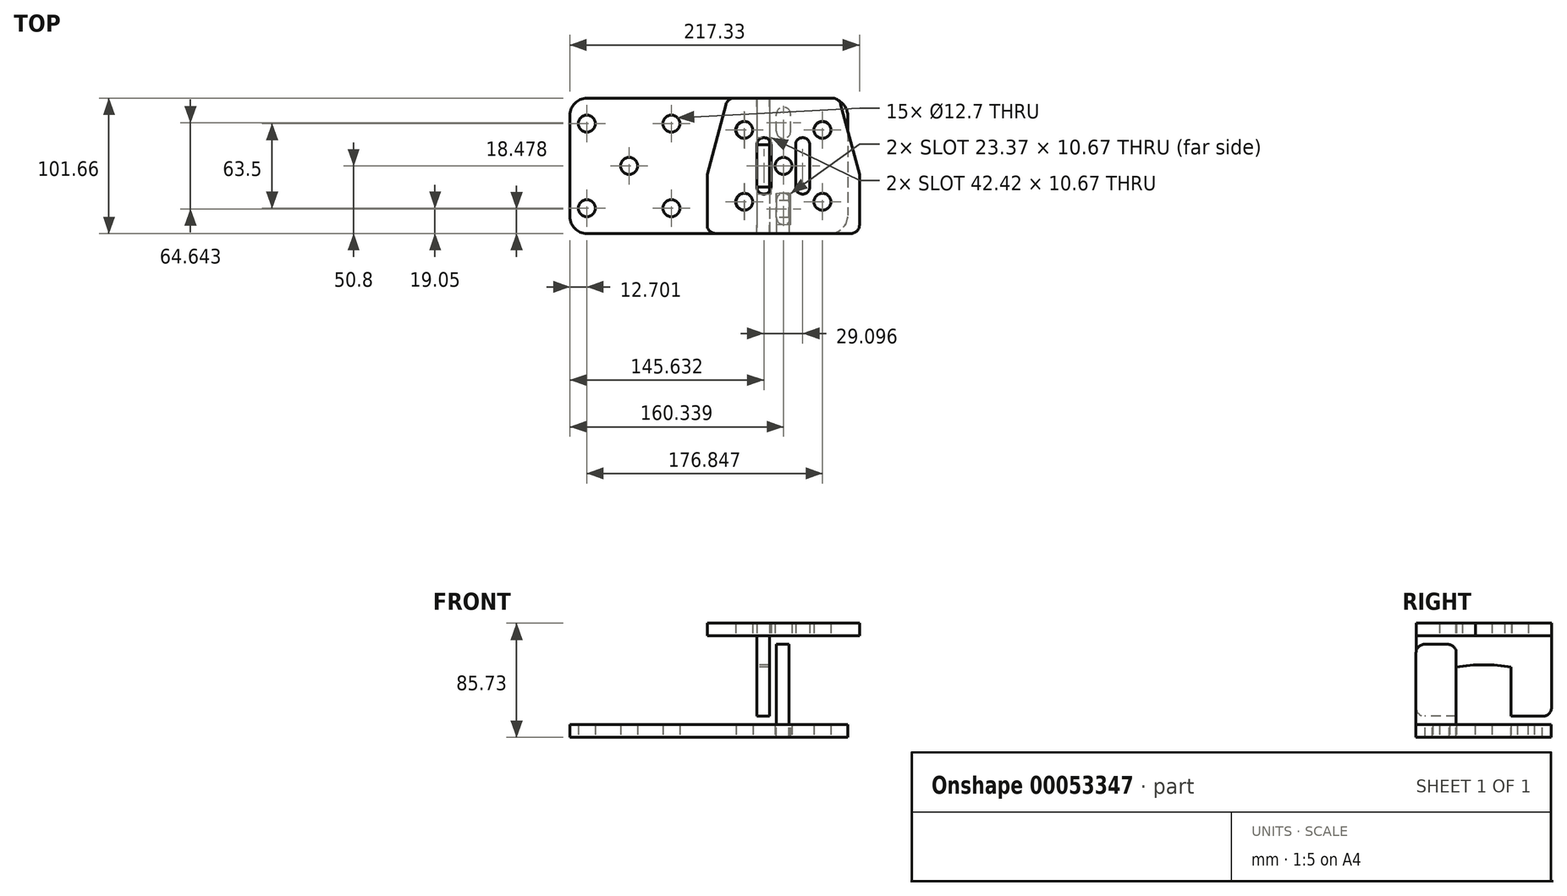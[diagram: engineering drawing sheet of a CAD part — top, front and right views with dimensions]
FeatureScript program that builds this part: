
annotation { "Feature Type Name" : "Feature", "Feature Type Description" : "" }
export const myFeature = defineFeature(function(context is Context, id is Id, definition is map)
    precondition{}
    {
        {
            var Q0;
            Q0=qCreatedBy(makeId("Top.planeOp"),FACE);
            var sketch = newSketch(context, id + "F0", { "sketchPlane" : qUnion([Q0])});
            skLineSegment(sketch, "E0.bottom", {"start": v(-84.85, -50.8) * mm, "end": v(97.55, -50.8) * mm});
            skLineSegment(sketch, "E0.top", {"start": v(-84.85, 50.8) * mm, "end": v(97.55, 50.8) * mm});
            skPoint(sketch, "E0.middle", {"position": v(0, 0) * mm});
            skCircle(sketch, "E1", {"center": v(-84.85, 31.75) * mm, "radius": 6.35 * mm});
            skCircle(sketch, "E2.0.1.0", {"center": v(-84.85, -31.75) * mm, "radius": 6.35 * mm});
            skCircle(sketch, "E2.1.0.0", {"center": v(-21.35, 31.75) * mm, "radius": 6.35 * mm});
            skCircle(sketch, "E2.1.1.0", {"center": v(-21.35, -31.75) * mm, "radius": 6.35 * mm});
            skLineSegment(sketch, "E2.direction1", {"start": v(-84.85, 31.75) * mm, "end": v(-21.35, 31.75) * mm, "construction": true});
            skLineSegment(sketch, "E2.direction2", {"start": v(-84.85, 31.75) * mm, "end": v(-84.85, -31.75) * mm, "construction": true});
            skLineSegment(sketch, "E3", {"start": v(-97.55, 0) * mm, "end": v(-84.85, 0) * mm, "construction": true});
            skPoint(sketch, "E4.visualSharp", {"position": v(-97.55, -50.8) * mm});
            skArc(sketch, "E4.filletArc", {"start": v(-97.55, -38.1) * mm, "mid": v(-93.83, -47.08) * mm, "end": v(-84.85, -50.8) * mm});
            skCircle(sketch, "E5", {"center": v(33.58, 26.92) * mm, "radius": 6.35 * mm});
            skCircle(sketch, "E6.0.1.0", {"center": v(33.58, -26.92) * mm, "radius": 6.35 * mm});
            skCircle(sketch, "E6.1.0.0", {"center": v(92, 26.92) * mm, "radius": 6.35 * mm});
            skCircle(sketch, "E6.1.1.0", {"center": v(92, -26.92) * mm, "radius": 6.35 * mm});
            skLineSegment(sketch, "E6.direction1", {"start": v(33.58, 26.92) * mm, "end": v(92, 26.92) * mm, "construction": true});
            skLineSegment(sketch, "E6.direction2", {"start": v(33.58, 26.92) * mm, "end": v(33.58, -26.92) * mm, "construction": true});
            skLineSegment(sketch, "E7", {"start": v(400.93, 50.8) * mm, "end": v(400.93, -50.8) * mm, "construction": true});
            skCircle(sketch, "E8", {"center": v(-53.1, 0) * mm, "radius": 6.35 * mm});
            skCircle(sketch, "E9", {"center": v(62.79, 0) * mm, "radius": 6.35 * mm});
            skPoint(sketch, "E9.centerSnap0", {"position": v(33.58, 0) * mm});
            skPoint(sketch, "E10", {"position": v(-53.1, 31.75) * mm});
            skPoint(sketch, "E11", {"position": v(62.79, 26.92) * mm});
            skCircle(sketch, "E12.MirrorC", {"center": v(854.95, 0) * mm, "radius": 6.35 * mm});
            skCircle(sketch, "E13.MirrorC", {"center": v(768.27, 26.92) * mm, "radius": 6.35 * mm});
            skArc(sketch, "E14.MirrorCS", {"start": v(899.4, -38.1) * mm, "mid": v(895.68, -47.08) * mm, "end": v(886.7, -50.8) * mm});
            skLineSegment(sketch, "E15.MirrorCS", {"start": v(899.4, 0) * mm, "end": v(886.7, 0) * mm, "construction": true});
            skLineSegment(sketch, "E16.MirrorCS", {"start": v(886.7, 31.75) * mm, "end": v(823.2, 31.75) * mm, "construction": true});
            skLineSegment(sketch, "E17.MirrorCS", {"start": v(768.27, 26.92) * mm, "end": v(709.85, 26.92) * mm, "construction": true});
            skCircle(sketch, "E18.MirrorC", {"center": v(823.2, -31.75) * mm, "radius": 6.35 * mm});
            skPoint(sketch, "E19.MirrorP", {"position": v(768.27, 0) * mm});
            skCircle(sketch, "E20.MirrorC", {"center": v(823.2, 31.75) * mm, "radius": 6.35 * mm});
            skCircle(sketch, "E21.MirrorC", {"center": v(886.7, -31.75) * mm, "radius": 6.35 * mm});
            skCircle(sketch, "E22.MirrorC", {"center": v(886.7, 31.75) * mm, "radius": 6.35 * mm});
            skPoint(sketch, "E23.MirrorP", {"position": v(739.06, 26.92) * mm});
            skLineSegment(sketch, "E24.MirrorCS", {"start": v(704.3, -50.8) * mm, "end": v(704.3, 50.8) * mm});
            skLineSegment(sketch, "E25.MirrorCS", {"start": v(899.4, -38.1) * mm, "end": v(899.4, 50.8) * mm});
            skPoint(sketch, "E26.MirrorP", {"position": v(854.95, 31.75) * mm});
            skLineSegment(sketch, "E27.MirrorCS", {"start": v(899.4, 50.8) * mm, "end": v(704.3, 50.8) * mm});
            skCircle(sketch, "E28.MirrorC", {"center": v(739.06, 0) * mm, "radius": 6.35 * mm});
            skCircle(sketch, "E29.MirrorC", {"center": v(709.85, -26.92) * mm, "radius": 6.35 * mm});
            skPoint(sketch, "E30.MirrorP", {"position": v(899.4, -50.8) * mm});
            skCircle(sketch, "E31.MirrorC", {"center": v(768.27, -26.92) * mm, "radius": 6.35 * mm});
            skLineSegment(sketch, "E32.MirrorCS", {"start": v(886.7, 31.75) * mm, "end": v(886.7, -31.75) * mm, "construction": true});
            skLineSegment(sketch, "E33.MirrorCS", {"start": v(768.27, 26.92) * mm, "end": v(768.27, -26.92) * mm, "construction": true});
            skCircle(sketch, "E34.MirrorC", {"center": v(709.85, 26.92) * mm, "radius": 6.35 * mm});
            skPoint(sketch, "E35.MirrorP", {"position": v(801.85, 0) * mm});
            skLineSegment(sketch, "E36.MirrorCS", {"start": v(886.7, -50.8) * mm, "end": v(704.3, -50.8) * mm});
            skLineSegment(sketch, "E37", {"start": v(111.05, 37.3) * mm, "end": v(111.05, -37.3) * mm});
            skArc(sketch, "E38", {"start": v(111.05, 37.3) * mm, "mid": v(107.1, 46.85) * mm, "end": v(97.55, 50.8) * mm});
            skArc(sketch, "E39", {"start": v(97.55, -50.8) * mm, "mid": v(107.1, -46.85) * mm, "end": v(111.05, -37.3) * mm});
            skCircle(sketch, "E40.MirrorC", {"center": v(972.43, 50.8) * mm, "radius": 6.35 * mm});
            skPoint(sketch, "E41.startSnap0", {"position": v(0, 50.8) * mm});
            skPoint(sketch, "E42.orphan", {"position": v(-97.55, 50.8) * mm});
            skPoint(sketch, "E43.visualSharp", {"position": v(-53.1, 50.8) * mm});
            skLineSegment(sketch, "E44", {"start": v(-97.55, -38.1) * mm, "end": v(-97.55, 38.1) * mm});
            skPoint(sketch, "E45.visualSharp", {"position": v(-97.55, 0) * mm});
            skArc(sketch, "E46.filletArc", {"start": v(-84.85, 50.8) * mm, "mid": v(-93.83, 47.08) * mm, "end": v(-97.55, 38.1) * mm});
            skSolve(sketch);
        }
        {
            var Q0;
            Q0=makeQuery(id+"F0.imprint","IMPRINT",FACE,{"disambiguationData":[TD([[makeQuery(id+"F0.imprint","IMPRINT",EDGE,{"derivedFrom":sQuery(id+"F0.wireOp",EDGE,"E0.bottom")}),1.0]])]});
            extrude(context, id + "F1", {"entities" : qUnion([Q0]), "depth" : 9.52 * mm});
        }
        {
            var Q0;
            Q0=makeQuery(id+"F1.opExtrude","CAP_FACE",FACE,{"disambiguationData":[OSD([sQuery(id+"F0.wireOp",EDGE,"E0.bottom"),sQuery(id+"F0.wireOp",EDGE,"E0.top"),sQuery(id+"F0.wireOp",EDGE,"E1"),sQuery(id+"F0.wireOp",EDGE,"E2.0.1.0"),sQuery(id+"F0.wireOp",EDGE,"E2.1.0.0"),sQuery(id+"F0.wireOp",EDGE,"E2.1.1.0"),sQuery(id+"F0.wireOp",EDGE,"E4.filletArc"),sQuery(id+"F0.wireOp",EDGE,"E5"),sQuery(id+"F0.wireOp",EDGE,"E6.0.1.0"),sQuery(id+"F0.wireOp",EDGE,"E6.1.0.0"),sQuery(id+"F0.wireOp",EDGE,"E6.1.1.0"),sQuery(id+"F0.wireOp",EDGE,"E8"),sQuery(id+"F0.wireOp",EDGE,"E9"),sQuery(id+"F0.wireOp",EDGE,"E37"),sQuery(id+"F0.wireOp",EDGE,"E38"),sQuery(id+"F0.wireOp",EDGE,"E39"),sQuery(id+"F0.wireOp",EDGE,"E44"),sQuery(id+"F0.wireOp",EDGE,"E46.filletArc")])],"isStart":false});
            var sketch = newSketch(context, id + "F2", { "sketchPlane" : qUnion([Q0])});
            skLineSegment(sketch, "E47", {"start": v(62.79, 25.97) * mm, "end": v(62.79, 38.67) * mm, "construction": true});
            skLineSegment(sketch, "E48", {"start": v(62.79, -38.67) * mm, "end": v(62.79, -25.97) * mm, "construction": true});
            skPoint(sketch, "E49.orphan", {"position": v(62.79, 0) * mm});
            skArc(sketch, "E50.0.startCap", {"start": v(68.12, 25.97) * mm, "mid": v(62.79, 20.64) * mm, "end": v(57.45, 25.97) * mm});
            skArc(sketch, "E50.0.endCap", {"start": v(57.45, 38.67) * mm, "mid": v(62.79, 44) * mm, "end": v(68.12, 38.67) * mm});
            skLineSegment(sketch, "E50.0.left", {"start": v(57.45, 25.97) * mm, "end": v(57.45, 38.67) * mm});
            skLineSegment(sketch, "E50.0.right", {"start": v(68.12, 25.97) * mm, "end": v(68.12, 38.67) * mm});
            skArc(sketch, "E50.1.startCap", {"start": v(68.12, -38.67) * mm, "mid": v(62.79, -44) * mm, "end": v(57.45, -38.67) * mm});
            skArc(sketch, "E50.1.endCap", {"start": v(57.45, -25.97) * mm, "mid": v(62.79, -20.64) * mm, "end": v(68.12, -25.97) * mm});
            skLineSegment(sketch, "E50.1.left", {"start": v(57.45, -38.67) * mm, "end": v(57.45, -25.97) * mm});
            skLineSegment(sketch, "E50.1.right", {"start": v(68.12, -38.67) * mm, "end": v(68.12, -25.97) * mm});
            skLineSegment(sketch, "E51.bottom", {"start": v(56.06, -20.64) * mm, "end": v(69.52, -20.64) * mm, "construction": true});
            skLineSegment(sketch, "E51.top", {"start": v(56.06, 20.64) * mm, "end": v(69.52, 20.64) * mm, "construction": true});
            skLineSegment(sketch, "E51.left", {"start": v(56.06, -20.64) * mm, "end": v(56.06, 20.64) * mm, "construction": true});
            skLineSegment(sketch, "E51.right", {"start": v(69.52, -20.64) * mm, "end": v(69.52, 20.64) * mm, "construction": true});
            skSolve(sketch);
        }
        {
            var Q0;
            Q0 = qSketchRegion(id + "F2", true);
            extrude(context, id + "F3", {"entities" : qUnion([Q0]), "operationType" : NewBodyOperationType.REMOVE, "oppositeDirection" : true, "depth" : 25.4 * mm});
        }
        {
            var Q0;
            Q0=qCreatedBy(makeId("Top.planeOp"),FACE);
            cPlane(context, id + "F4", {"entities" : qUnion([Q0]), "cplaneType" : CPlaneType.OFFSET, "offset" : 76.2 * mm, "width" : 152.4 * mm, "height" : 152.4 * mm});
        }
        {
            var Q0;
            Q0=qCreatedBy(id+"F4.planeOp",FACE);
            var sketch = newSketch(context, id + "F5", { "sketchPlane" : qUnion([Q0])});
            skArc(sketch, "E52", {"start": v(25.67, 50.86) * mm, "mid": v(21.8, 49.55) * mm, "end": v(19.53, 46.16) * mm});
            skArc(sketch, "E53", {"start": v(105.73, 46.16) * mm, "mid": v(103.46, 49.55) * mm, "end": v(99.6, 50.86) * mm});
            skArc(sketch, "E54", {"start": v(5.48, -44.39) * mm, "mid": v(7.34, -48.88) * mm, "end": v(11.83, -50.74) * mm});
            skArc(sketch, "E55", {"start": v(113.43, -50.74) * mm, "mid": v(117.92, -48.88) * mm, "end": v(119.78, -44.39) * mm});
            skCircle(sketch, "E56", {"center": v(62.79, 0) * mm, "radius": 6.35 * mm});
            skCircle(sketch, "E57", {"center": v(33.26, 27.05) * mm, "radius": 6.35 * mm});
            skCircle(sketch, "E58", {"center": v(92, 27.05) * mm, "radius": 6.35 * mm});
            skCircle(sketch, "E59", {"center": v(33.26, -26.92) * mm, "radius": 6.35 * mm});
            skCircle(sketch, "E60", {"center": v(92, -26.92) * mm, "radius": 6.35 * mm});
            skLineSegment(sketch, "E61", {"start": v(113.43, -50.74) * mm, "end": v(11.83, -50.74) * mm});
            skLineSegment(sketch, "E62", {"start": v(99.6, 50.86) * mm, "end": v(25.67, 50.86) * mm});
            skLineSegment(sketch, "E63", {"start": v(5.48, -44.39) * mm, "end": v(5.48, -6.29) * mm});
            skLineSegment(sketch, "E64", {"start": v(119.78, -44.39) * mm, "end": v(119.78, -6.29) * mm});
            skLineSegment(sketch, "E65", {"start": v(19.53, 46.16) * mm, "end": v(5.48, -6.29) * mm});
            skLineSegment(sketch, "E66", {"start": v(105.73, 46.16) * mm, "end": v(119.78, -6.29) * mm});
            skPoint(sketch, "E67", {"position": v(62.63, 50.86) * mm});
            skSolve(sketch);
        }
        {
            var Q0;
            Q0 = qSketchRegion(id + "F5", true);
            extrude(context, id + "F6", {"entities" : qUnion([Q0]), "depth" : 9.52 * mm});
        }
        {
            var Q0;
            Q0=makeQuery(id+"F6.opExtrude","CAP_FACE",FACE,{"disambiguationData":[OSD([sQuery(id+"F5.wireOp",EDGE,"E52"),sQuery(id+"F5.wireOp",EDGE,"E53"),sQuery(id+"F5.wireOp",EDGE,"E54"),sQuery(id+"F5.wireOp",EDGE,"E55"),sQuery(id+"F5.wireOp",EDGE,"E56"),sQuery(id+"F5.wireOp",EDGE,"E57"),sQuery(id+"F5.wireOp",EDGE,"E58"),sQuery(id+"F5.wireOp",EDGE,"E59"),sQuery(id+"F5.wireOp",EDGE,"E60"),sQuery(id+"F5.wireOp",EDGE,"E61"),sQuery(id+"F5.wireOp",EDGE,"E62"),sQuery(id+"F5.wireOp",EDGE,"E63"),sQuery(id+"F5.wireOp",EDGE,"E64"),sQuery(id+"F5.wireOp",EDGE,"E65"),sQuery(id+"F5.wireOp",EDGE,"E66")])],"isStart":true});
            var sketch = newSketch(context, id + "F7", { "sketchPlane" : qUnion([Q0])});
            skLineSegment(sketch, "E68", {"start": v(77.18, -15.88) * mm, "end": v(77.18, 15.88) * mm, "construction": true});
            skLineSegment(sketch, "E69", {"start": v(62.63, 50.74) * mm, "end": v(62.63, -50.86) * mm, "construction": true});
            skPoint(sketch, "E70", {"position": v(77.18, 0) * mm});
            skArc(sketch, "E71.0.startCap", {"start": v(82.51, -15.88) * mm, "mid": v(77.18, -21.2) * mm, "end": v(71.84, -15.88) * mm});
            skArc(sketch, "E71.0.endCap", {"start": v(71.84, 15.88) * mm, "mid": v(77.18, 21.2) * mm, "end": v(82.51, 15.88) * mm});
            skLineSegment(sketch, "E71.0.left", {"start": v(71.84, -15.88) * mm, "end": v(71.84, 15.88) * mm});
            skLineSegment(sketch, "E71.0.right", {"start": v(82.51, -15.88) * mm, "end": v(82.51, 15.88) * mm});
            skLineSegment(sketch, "E72", {"start": v(98.31, -27.75) * mm, "end": v(85.69, -27.75) * mm, "construction": true});
            skLineSegment(sketch, "E73.MirrorCS", {"start": v(53.42, -15.88) * mm, "end": v(53.42, 15.88) * mm});
            skArc(sketch, "E74.MirrorCS", {"start": v(42.75, -15.88) * mm, "mid": v(48.08, -21.2) * mm, "end": v(53.42, -15.88) * mm});
            skLineSegment(sketch, "E75.MirrorCS", {"start": v(42.75, -15.88) * mm, "end": v(42.75, 15.88) * mm});
            skArc(sketch, "E76.MirrorCS", {"start": v(53.42, 15.88) * mm, "mid": v(48.08, 21.2) * mm, "end": v(42.75, 15.88) * mm});
            skSolve(sketch);
        }
        {
            var Q0;
            Q0 = qSketchRegion(id + "F7", true);
            extrude(context, id + "F8", {"entities" : qUnion([Q0]), "operationType" : NewBodyOperationType.REMOVE, "oppositeDirection" : true, "depth" : 25.4 * mm});
        }
        {
            var Q0;
            Q0=makeQuery(id+"F8.boolean.opBoolean","COPY",FACE,{"derivedFrom":makeQuery(id+"F8.opExtrude","SWEPT_FACE",FACE,{"disambiguationData":[OSD([sQuery(id+"F7.wireOp",EDGE,"E75.MirrorCS")])]})});
            var sketch = newSketch(context, id + "F9", { "sketchPlane" : qUnion([Q0])});
            skLineSegment(sketch, "E77", {"start": v(15.88, 85.73) * mm, "end": v(15.88, 76.2) * mm});
            skLineSegment(sketch, "E78", {"start": v(-15.88, 85.73) * mm, "end": v(15.88, 85.73) * mm});
            skLineSegment(sketch, "E79", {"start": v(-15.88, 85.73) * mm, "end": v(-15.88, 76.2) * mm});
            skLineSegment(sketch, "E80", {"start": v(-15.88, 76.2) * mm, "end": v(-50.74, 76.2) * mm});
            skLineSegment(sketch, "E81", {"start": v(50.86, 76.2) * mm, "end": v(15.88, 76.2) * mm});
            skPoint(sketch, "E82.end.orphan", {"position": v(-15.88, 76.2) * mm});
            skPoint(sketch, "E82.start.orphan", {"position": v(15.88, 76.2) * mm});
            skLineSegment(sketch, "E83", {"start": v(50.86, 76.2) * mm, "end": v(50.86, 22.23) * mm});
            skLineSegment(sketch, "E84", {"start": v(44.51, 15.87) * mm, "end": v(20.64, 15.87) * mm});
            skLineSegment(sketch, "E85", {"start": v(20.64, 15.87) * mm, "end": v(20.64, 52.87) * mm});
            skLineSegment(sketch, "E86", {"start": v(20.64, 52.87) * mm, "end": v(-20.64, 52.87) * mm, "construction": true});
            skLineSegment(sketch, "E87", {"start": v(-20.64, 52.87) * mm, "end": v(-20.64, 15.87) * mm});
            skLineSegment(sketch, "E88", {"start": v(-20.64, 15.87) * mm, "end": v(-44.39, 15.87) * mm});
            skLineSegment(sketch, "E89", {"start": v(-50.74, 22.23) * mm, "end": v(-50.74, 76.2) * mm});
            skPoint(sketch, "E90", {"position": v(0, 52.87) * mm});
            skPoint(sketch, "E91", {"position": v(0, 85.73) * mm});
            skArc(sketch, "E92", {"start": v(20.64, 52.87) * mm, "mid": v(0, 54.46) * mm, "end": v(-20.64, 52.87) * mm});
            skPoint(sketch, "E93.visualSharp", {"position": v(-50.74, 15.87) * mm});
            skArc(sketch, "E93.filletArc", {"start": v(-50.74, 22.23) * mm, "mid": v(-48.88, 17.73) * mm, "end": v(-44.39, 15.87) * mm});
            skPoint(sketch, "E94.visualSharp", {"position": v(50.86, 15.88) * mm});
            skArc(sketch, "E94.filletArc", {"start": v(44.51, 15.88) * mm, "mid": v(49, 17.73) * mm, "end": v(50.86, 22.23) * mm});
            skSolve(sketch);
        }
        {
            var Q0;
            Q0 = qSketchRegion(id + "F9", true);
            extrude(context, id + "F10", {"entities" : qUnion([Q0]), "depth" : 9.52 * mm});
        }
        {
            var Q0;
            Q0=makeQuery(id+"F3.boolean.opBoolean","COPY",FACE,{"derivedFrom":makeQuery(id+"F3.opExtrude","SWEPT_FACE",FACE,{"disambiguationData":[OSD([sQuery(id+"F2.wireOp",EDGE,"E50.1.left")])]})});
            var sketch = newSketch(context, id + "F11", { "sketchPlane" : qUnion([Q0])});
            skLineSegment(sketch, "E95", {"start": v(-25.97, 0) * mm, "end": v(-25.97, 9.52) * mm});
            skLineSegment(sketch, "E96", {"start": v(-25.97, 9.53) * mm, "end": v(-20.64, 9.53) * mm});
            skLineSegment(sketch, "E97", {"start": v(-38.67, 0) * mm, "end": v(-38.67, 9.52) * mm});
            skLineSegment(sketch, "E98", {"start": v(-38.67, 0) * mm, "end": v(-25.97, 0) * mm});
            skLineSegment(sketch, "E99", {"start": v(-38.67, 9.53) * mm, "end": v(-50.8, 9.53) * mm});
            skLineSegment(sketch, "E100.0", {"start": v(-20.64, 63.5) * mm, "end": v(-20.64, 9.52) * mm});
            skPoint(sketch, "E101.end.orphan", {"position": v(3.45, 9.53) * mm});
            skPoint(sketch, "E101.start.orphan", {"position": v(25.97, 9.53) * mm});
            skPoint(sketch, "E102.start.orphan", {"position": v(38.67, 9.53) * mm});
            skPoint(sketch, "E103.start.orphan", {"position": v(50.8, 9.53) * mm});
            skPoint(sketch, "E104.end.orphan", {"position": v(-25.97, 9.53) * mm});
            skPoint(sketch, "E104.start.orphan", {"position": v(-3.45, 9.53) * mm});
            skPoint(sketch, "E105.orphan", {"position": v(-20.64, 15.87) * mm});
            skLineSegment(sketch, "E106", {"start": v(-26.99, 69.85) * mm, "end": v(-44.45, 69.85) * mm});
            skLineSegment(sketch, "E107", {"start": v(-50.8, 63.5) * mm, "end": v(-50.8, 9.52) * mm});
            skPoint(sketch, "E108.orphan", {"position": v(-20.64, 52.87) * mm});
            skPoint(sketch, "E109.end.orphan", {"position": v(-38.67, 9.53) * mm});
            skPoint(sketch, "E110.visualSharp", {"position": v(-50.8, 69.85) * mm});
            skArc(sketch, "E110.filletArc", {"start": v(-44.45, 69.85) * mm, "mid": v(-48.94, 68) * mm, "end": v(-50.8, 63.5) * mm});
            skPoint(sketch, "E111.visualSharp", {"position": v(-20.64, 69.85) * mm});
            skArc(sketch, "E111.filletArc", {"start": v(-20.64, 63.5) * mm, "mid": v(-22.5, 68) * mm, "end": v(-26.99, 69.85) * mm});
            skSolve(sketch);
        }
        {
            var Q0;
            Q0 = qSketchRegion(id + "F11", true);
            extrude(context, id + "F12", {"entities" : qUnion([Q0]), "depth" : 9.52 * mm});
        }
    });
